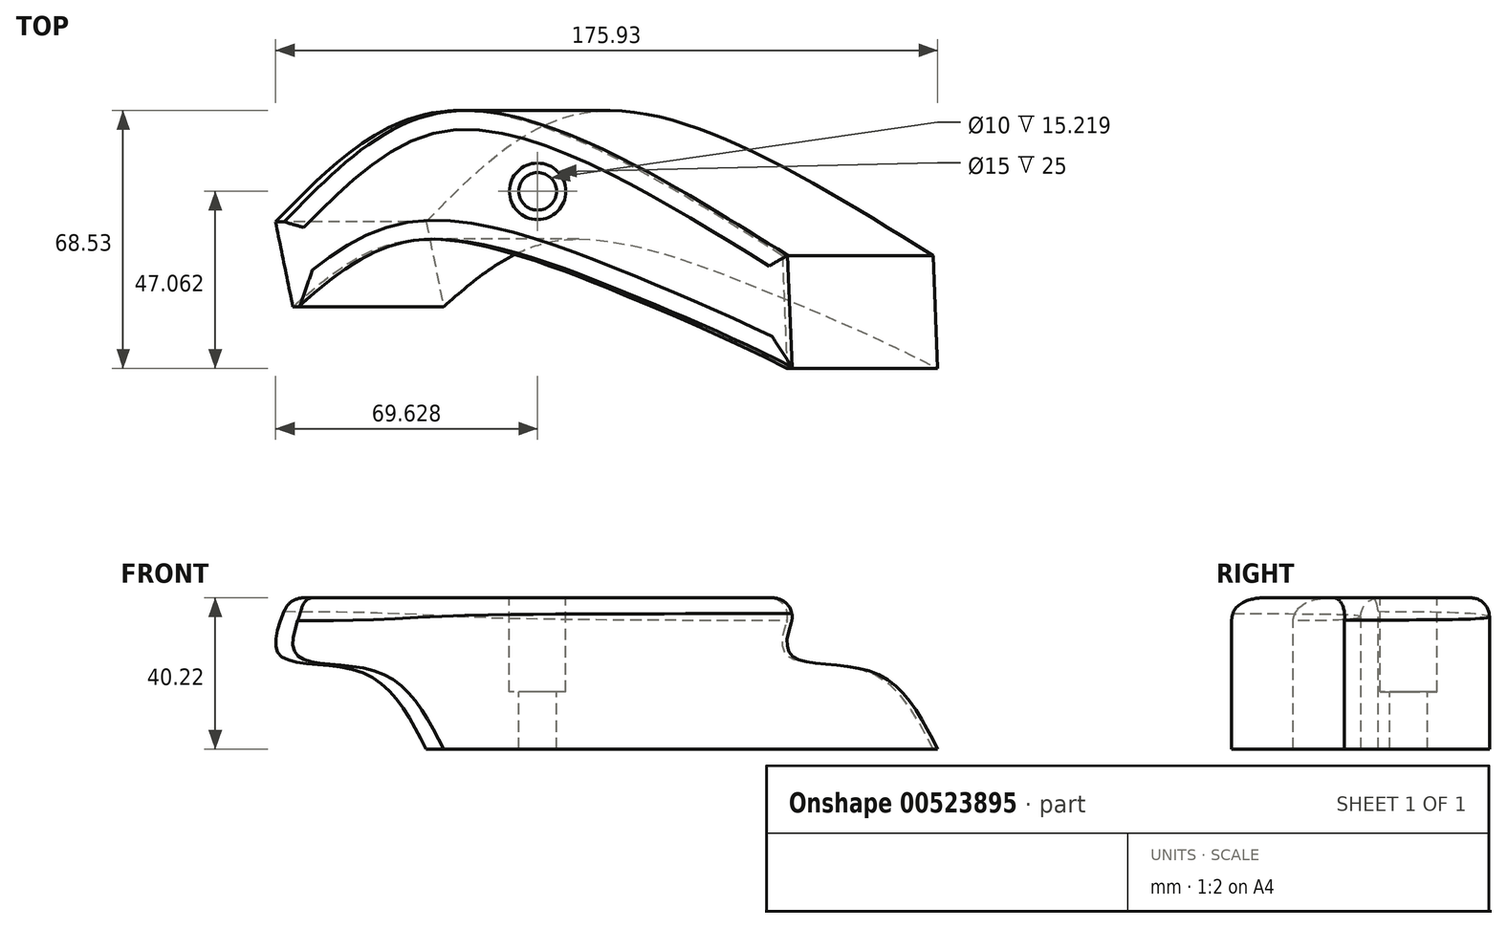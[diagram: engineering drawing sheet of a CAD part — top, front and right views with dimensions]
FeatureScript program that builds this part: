
annotation { "Feature Type Name" : "Feature", "Feature Type Description" : "" }
export const myFeature = defineFeature(function(context is Context, id is Id, definition is map)
    precondition{}
    {
        {
            var Q0;
            Q0=qCreatedBy(makeId("Top.planeOp"),FACE);
            var sketch = newSketch(context, id + "F0", { "sketchPlane" : qUnion([Q0])});
            skFitSpline(sketch, "E0", {"points": [v(-49.15, -18.61) * mm, v(-3.91, 10.83) * mm, v(85.5, -27.58) * mm], "startDerivative": vector(95.3, 98.02) * mm, "endDerivative": vector(170.34, -106) * mm});
            skFitSpline(sketch, "E1", {"points": [v(-44.56, -41.15) * mm, v(-14.05, -23.57) * mm, v(39.24, -36.3) * mm, v(86.73, -57.55) * mm], "startDerivative": vector(94.94, 82.36) * mm, "endDerivative": vector(128.18, -65.28) * mm});
            skLineSegment(sketch, "E2", {"start": v(-49.15, -18.61) * mm, "end": v(-44.56, -41.15) * mm});
            skLineSegment(sketch, "E3", {"start": v(85.5, -27.58) * mm, "end": v(86.73, -57.55) * mm});
            skSolve(sketch);
        }
        {
            var Q0;
            Q0=qCreatedBy(makeId("Front.planeOp"),FACE);
            var sketch = newSketch(context, id + "F1", { "sketchPlane" : qUnion([Q0])});
            skFitSpline(sketch, "E4", {"points": [v(0, 0) * mm, v(-17.13, 20.38) * mm, v(-38.95, 25.02) * mm, v(-36.26, 40.22) * mm], "startDerivative": vector(-35.28, 69) * mm, "endDerivative": vector(28.25, 65.47) * mm});
            skSolve(sketch);
        }
        {
            var Q0;
            Q0 = qSketchRegion(id + "F0", true);
            var Q1;
            Q1 = qConstructionFilter(qBodyType(qCreatedBy(id + "F1" ,EDGE), BodyType.WIRE), ConstructionObject.NO);
            sweep(context, id + "F2", {"profiles" : qUnion([Q0]), "path" : qUnion([Q1]), "keepProfileOrientation" : true});
        }
        {
            var Q0;
            Q0=makeQuery(id+"F2.opSweep","CAP_FACE",FACE,{"disambiguationData":[OSD([sQuery(id+"F0.wireOp",EDGE,"E0"),sQuery(id+"F0.wireOp",EDGE,"E1"),sQuery(id+"F0.wireOp",EDGE,"E2"),sQuery(id+"F0.wireOp",EDGE,"E3"),sQuery(id+"F1.wireOp",VERTEX,"E4.end")])],"isStart":false});
            fillet(context, id + "F3", {"entities" : qUnion([Q0]), "radius" : 5 * mm, "tangentPropagation" : true, "allowEdgeOverflow" : false});
        }
        {
            var Q0;
            Q0=makeQuery(id+"F2.opSweep","CAP_FACE",FACE,{"disambiguationData":[OSD([sQuery(id+"F0.wireOp",EDGE,"E0"),sQuery(id+"F0.wireOp",EDGE,"E1"),sQuery(id+"F0.wireOp",EDGE,"E2"),sQuery(id+"F0.wireOp",EDGE,"E3"),sQuery(id+"F1.wireOp",VERTEX,"E4.end")])],"isStart":false});
            var sketch = newSketch(context, id + "F4", { "sketchPlane" : qUnion([Q0])});
            skPoint(sketch, "E5", {"position": v(-19.57, -10.49) * mm});
            skSolve(sketch);
        }
        {
            var Q0;
            Q0=sQuery(id+"F4.wireOp",VERTEX,"E5");
            var Q1;
            Q1=makeQuery(id+"F2.opSweep","SWEPT_BODY",BODY,{"disambiguationData":[OSD([sQuery(id+"F0.wireOp",EDGE,"E0"),sQuery(id+"F0.wireOp",EDGE,"E1"),sQuery(id+"F0.wireOp",EDGE,"E2"),sQuery(id+"F0.wireOp",EDGE,"E3"),sQuery(id+"F1.wireOp",EDGE,"E4")])]});
            hole(context, id + "F5", {"style" : HoleStyle.C_BORE, "endStyle" : HoleEndStyle.THROUGH, "holeDiameter" : 10 * mm, "cBoreDiameter" : 15 * mm, "cBoreDepth" : 25 * mm, "isTappedThrough" : true, "tappedDepth" : 12 * mm, "tapClearance" : 3, "startFromSketch" : true, "locations" : qUnion([Q0]), "scope" : qUnion([Q1])});
        }
    });
